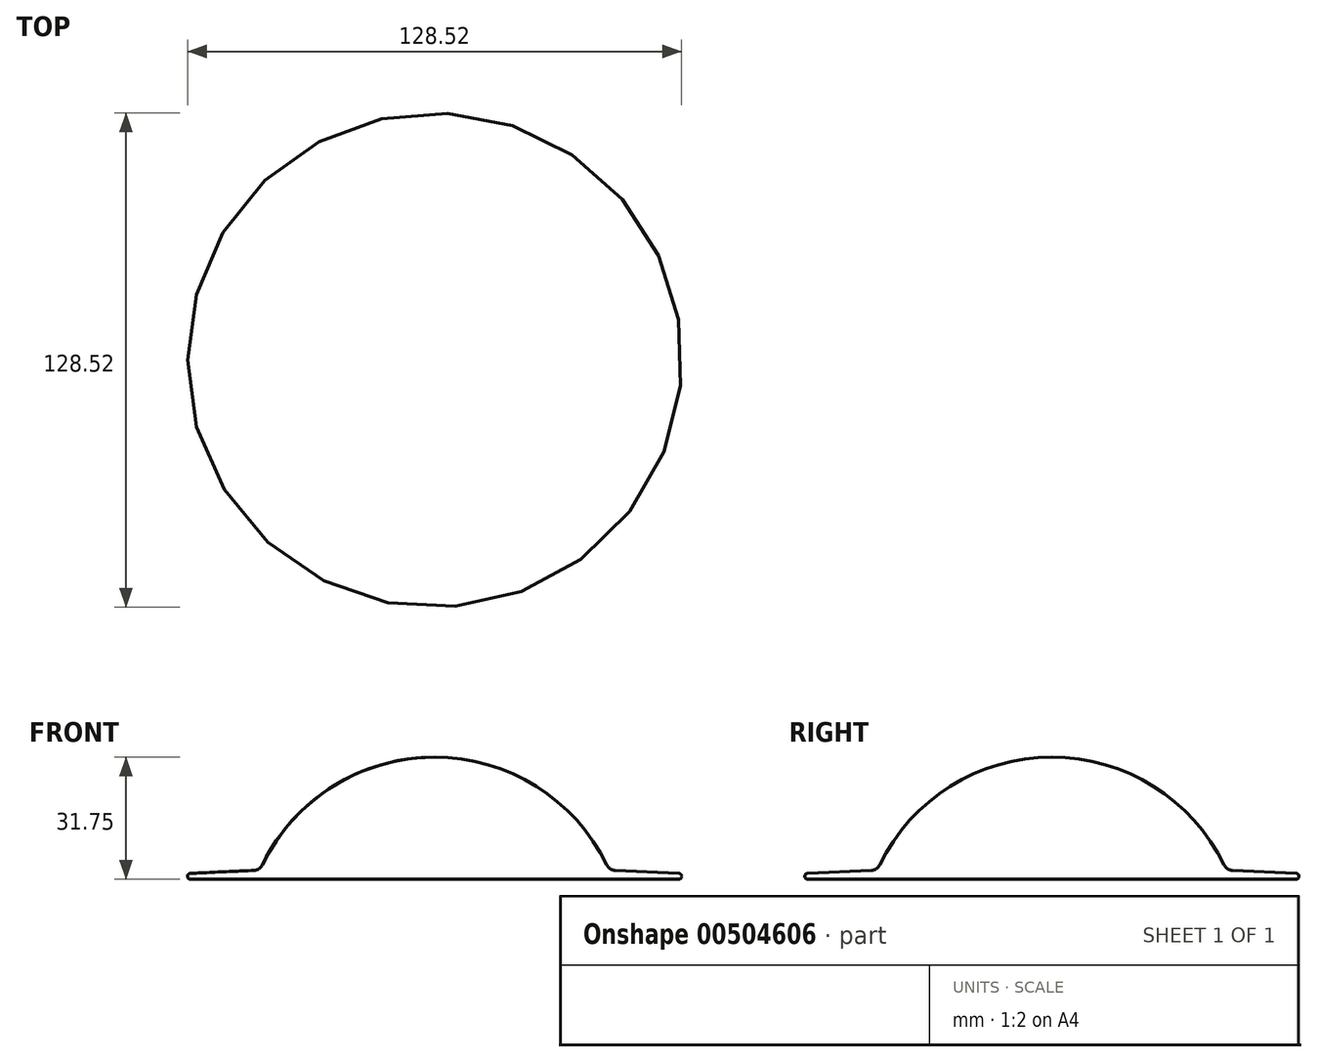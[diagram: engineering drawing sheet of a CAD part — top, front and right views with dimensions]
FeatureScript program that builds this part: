
annotation { "Feature Type Name" : "Feature", "Feature Type Description" : "" }
export const myFeature = defineFeature(function(context is Context, id is Id, definition is map)
    precondition{}
    {
        {
            var Q0;
            Q0=qCreatedBy(makeId("Front.planeOp"),FACE);
            var sketch = newSketch(context, id + "F0", { "sketchPlane" : qUnion([Q0])});
            skLineSegment(sketch, "E0", {"start": v(-63.54, 1.52) * mm, "end": v(-46.97, 2.29) * mm});
            skArc(sketch, "E1", {"start": v(0, 31.75) * mm, "mid": v(-26.42, 24.16) * mm, "end": v(-44.8, 3.71) * mm});
            skLineSegment(sketch, "E2", {"start": v(0, 0) * mm, "end": v(-63.5, 0) * mm});
            skLineSegment(sketch, "E3", {"start": v(0, 0) * mm, "end": v(0, 63.3) * mm, "construction": true});
            skPoint(sketch, "E3.endSnap0", {"position": v(0, 31.75) * mm});
            skPoint(sketch, "E4.visualSharp", {"position": v(-96.57, 0) * mm});
            skArc(sketch, "E4.filletArc", {"start": v(-63.54, 1.52) * mm, "mid": v(-64.26, 0.74) * mm, "end": v(-63.5, 0) * mm});
            skLineSegment(sketch, "E5", {"start": v(0, 31.75) * mm, "end": v(0, 0) * mm});
            skPoint(sketch, "E6.visualSharp", {"position": v(-45.43, 2.36) * mm});
            skArc(sketch, "E6.filletArc", {"start": v(-46.97, 2.29) * mm, "mid": v(-45.69, 2.7) * mm, "end": v(-44.8, 3.71) * mm});
            skSolve(sketch);
        }
        {
            var Q0;
            Q0=makeQuery(id+"F0.imprint","IMPRINT",FACE,{"disambiguationData":[TD([[makeQuery(id+"F0.imprint","IMPRINT",EDGE,{"derivedFrom":sQuery(id+"F0.wireOp",EDGE,"E0")}),-1.0]])]});
            var Q1;
            Q1=sQuery(id+"F0.wireOp",EDGE,"E3");
            revolve(context, id + "F1", {"entities" : qUnion([Q0]), "axis" : qUnion([Q1]), "revolveType" : RevolveType.FULL});
        }
    });
